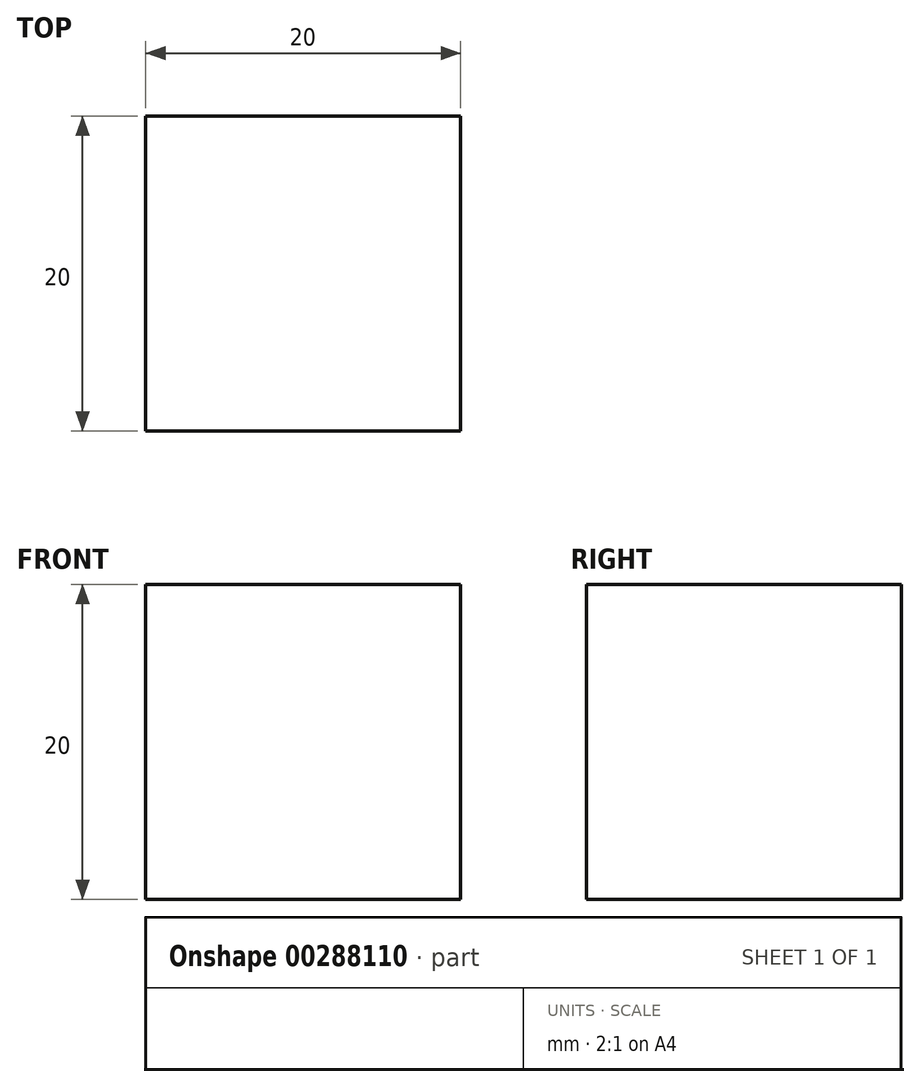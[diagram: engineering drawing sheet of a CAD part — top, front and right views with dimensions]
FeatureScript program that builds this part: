
annotation { "Feature Type Name" : "Feature", "Feature Type Description" : "" }
export const myFeature = defineFeature(function(context is Context, id is Id, definition is map)
    precondition{}
    {
        {
            var Q0;
            Q0=qCreatedBy(makeId("Top.planeOp"),FACE);
            var sketch = newSketch(context, id + "F0", { "sketchPlane" : qUnion([Q0])});
            skLineSegment(sketch, "E0.bottom", {"start": v(10, -10) * mm, "end": v(-10, -10) * mm});
            skLineSegment(sketch, "E0.top", {"start": v(10, 10) * mm, "end": v(-10, 10) * mm});
            skLineSegment(sketch, "E0.left", {"start": v(10, -10) * mm, "end": v(10, 10) * mm});
            skLineSegment(sketch, "E0.right", {"start": v(-10, -10) * mm, "end": v(-10, 10) * mm});
            skPoint(sketch, "E0.middle", {"position": v(0, 0) * mm});
            skSolve(sketch);
        }
        {
            var Q0;
            Q0=makeQuery(id+"F0.imprint","IMPRINT",FACE,{"disambiguationData":[TD([[makeQuery(id+"F0.imprint","IMPRINT",EDGE,{"derivedFrom":sQuery(id+"F0.wireOp",EDGE,"E0.bottom")}),-1.0]])]});
            extrude(context, id + "F1", {"entities" : qUnion([Q0]), "depth" : 20 * mm});
        }
    });
